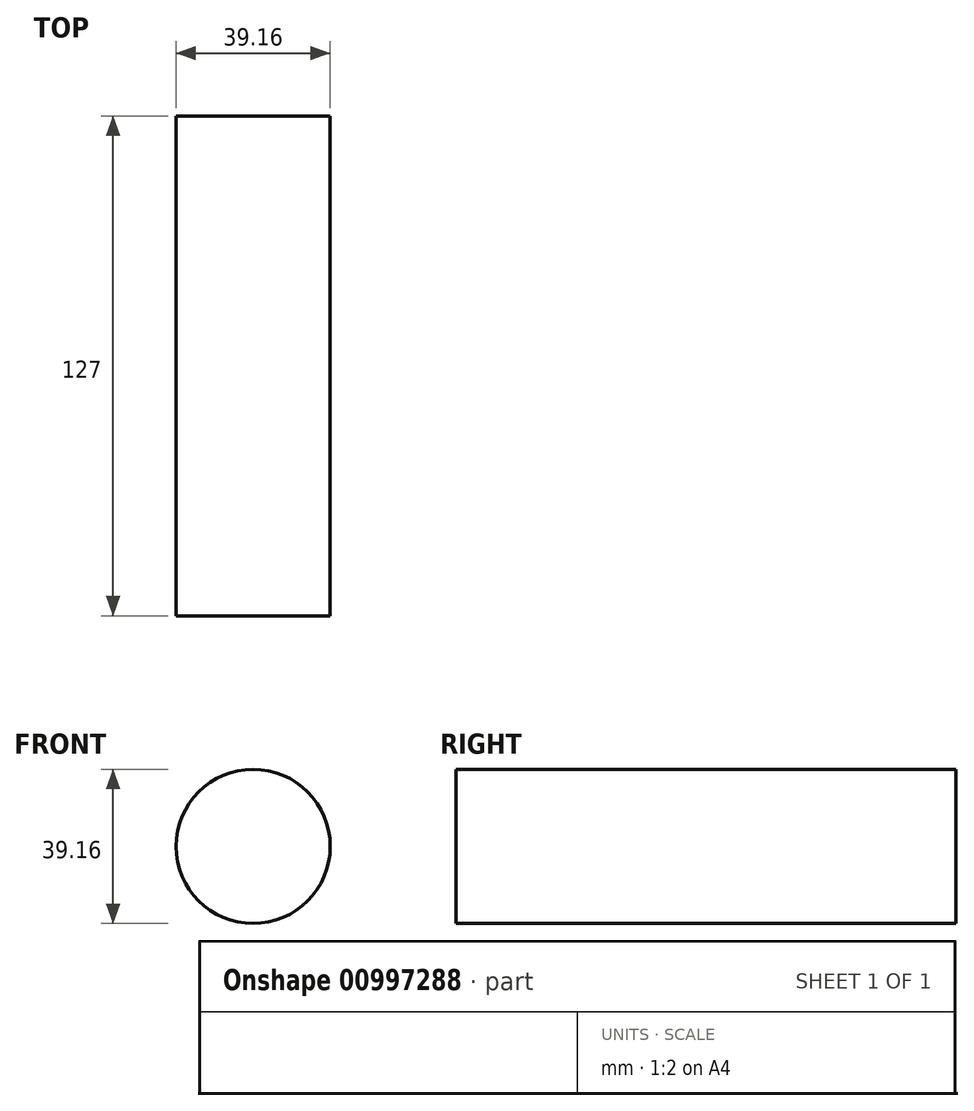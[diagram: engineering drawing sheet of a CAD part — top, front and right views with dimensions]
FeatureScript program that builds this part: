
annotation { "Feature Type Name" : "Feature", "Feature Type Description" : "" }
export const myFeature = defineFeature(function(context is Context, id is Id, definition is map)
    precondition{}
    {
        {
            var Q0;
            Q0=qCreatedBy(makeId("Front.planeOp"),FACE);
            var sketch = newSketch(context, id + "F0", { "sketchPlane" : qUnion([Q0])});
            skCircle(sketch, "E0", {"center": v(0, 0) * mm, "radius": 19.58 * mm});
            skSolve(sketch);
        }
        {
            var Q0;
            Q0 = qSketchRegion(id + "F0", true);
            extrude(context, id + "F1", {"entities" : qUnion([Q0]), "depth" : 127 * mm, "offsetDistance" : 25.4 * mm});
        }
    });
